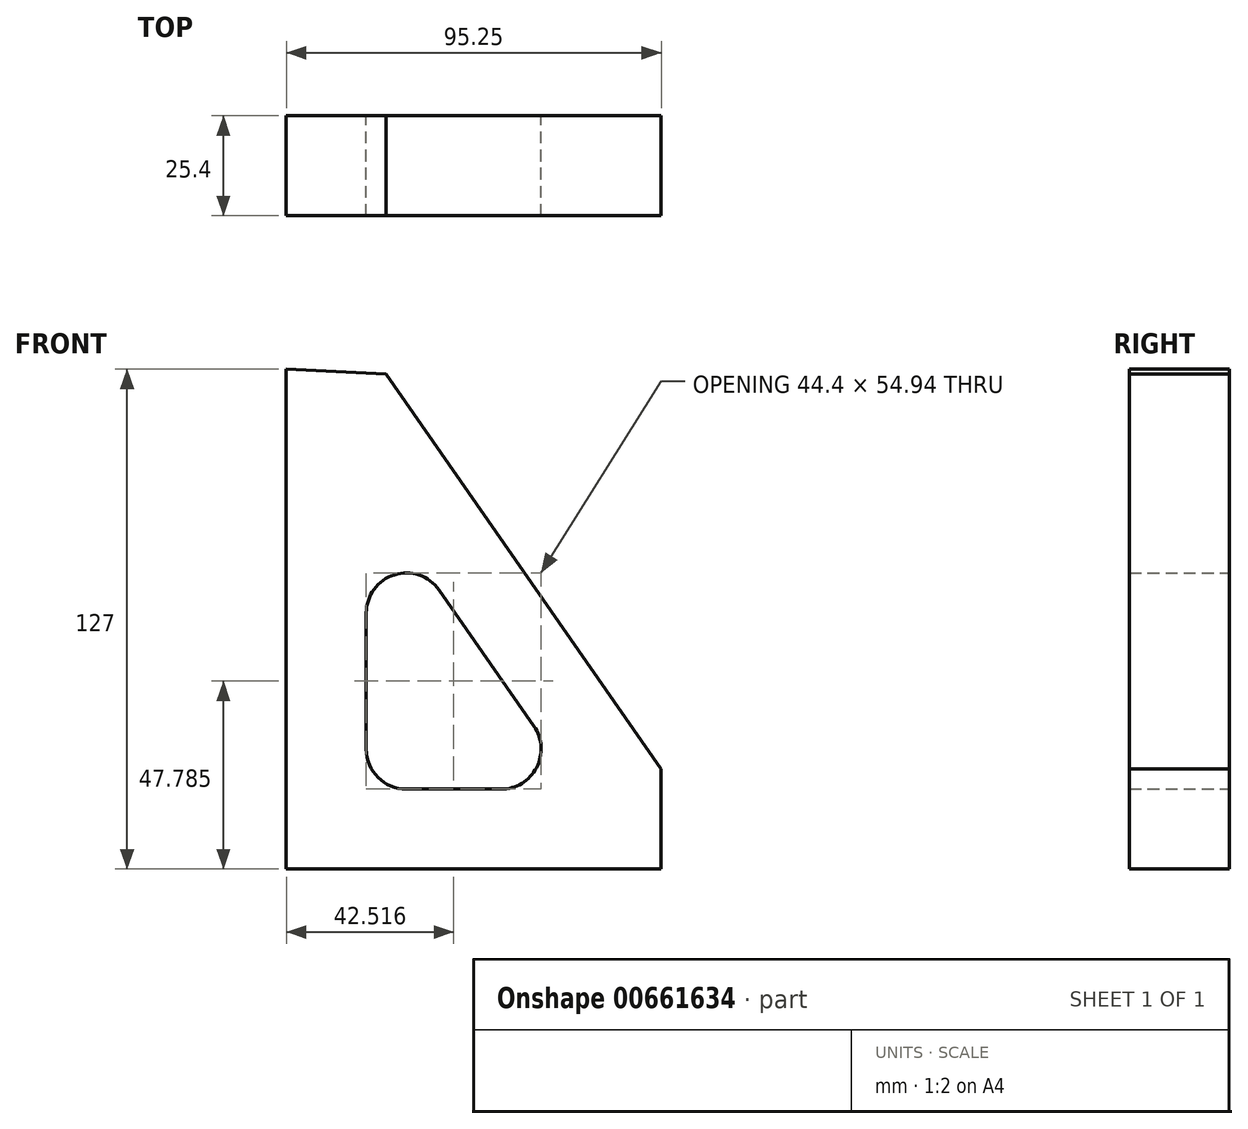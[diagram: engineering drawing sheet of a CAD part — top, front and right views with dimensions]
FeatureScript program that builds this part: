
annotation { "Feature Type Name" : "Feature", "Feature Type Description" : "" }
export const myFeature = defineFeature(function(context is Context, id is Id, definition is map)
    precondition{}
    {
        {
            var Q0;
            Q0=qCreatedBy(makeId("Front.planeOp"),FACE);
            var sketch = newSketch(context, id + "F0", { "sketchPlane" : qUnion([Q0])});
            skLineSegment(sketch, "E0", {"start": v(-33.67, 69.22) * mm, "end": v(-33.67, -57.78) * mm});
            skLineSegment(sketch, "E1", {"start": v(-33.67, -57.78) * mm, "end": v(61.58, -57.78) * mm});
            skLineSegment(sketch, "E2", {"start": v(61.58, -57.78) * mm, "end": v(61.58, -32.38) * mm});
            skLineSegment(sketch, "E3", {"start": v(61.58, -32.38) * mm, "end": v(-8.3, 68) * mm});
            skLineSegment(sketch, "E4", {"start": v(-8.3, 68) * mm, "end": v(-33.67, 69.22) * mm});
            skLineSegment(sketch, "E5.1", {"start": v(-3.2, -37.46) * mm, "end": v(20.9, -37.46) * mm});
            skLineSegment(sketch, "E5.2", {"start": v(29.24, -21.5) * mm, "end": v(5.15, 13.12) * mm});
            skLineSegment(sketch, "E5.4", {"start": v(-13.35, 7.32) * mm, "end": v(-13.35, -27.3) * mm});
            skArc(sketch, "E6.filletArc", {"start": v(5.15, 13.12) * mm, "mid": v(-6.23, 17) * mm, "end": v(-13.35, 7.32) * mm});
            skArc(sketch, "E7.filletArc", {"start": v(20.9, -37.46) * mm, "mid": v(29.9, -32) * mm, "end": v(29.24, -21.5) * mm});
            skPoint(sketch, "E8.visualSharp", {"position": v(-13.35, -37.46) * mm});
            skArc(sketch, "E8.filletArc", {"start": v(-13.35, -27.3) * mm, "mid": v(-10.38, -34.49) * mm, "end": v(-3.2, -37.46) * mm});
            skSolve(sketch);
        }
        {
            var Q0;
            Q0 = qSketchRegion(id + "F0", true);
            extrude(context, id + "F1", {"entities" : qUnion([Q0]), "depth" : 25.4 * mm, "offsetDistance" : 25.4 * mm});
        }
    });
